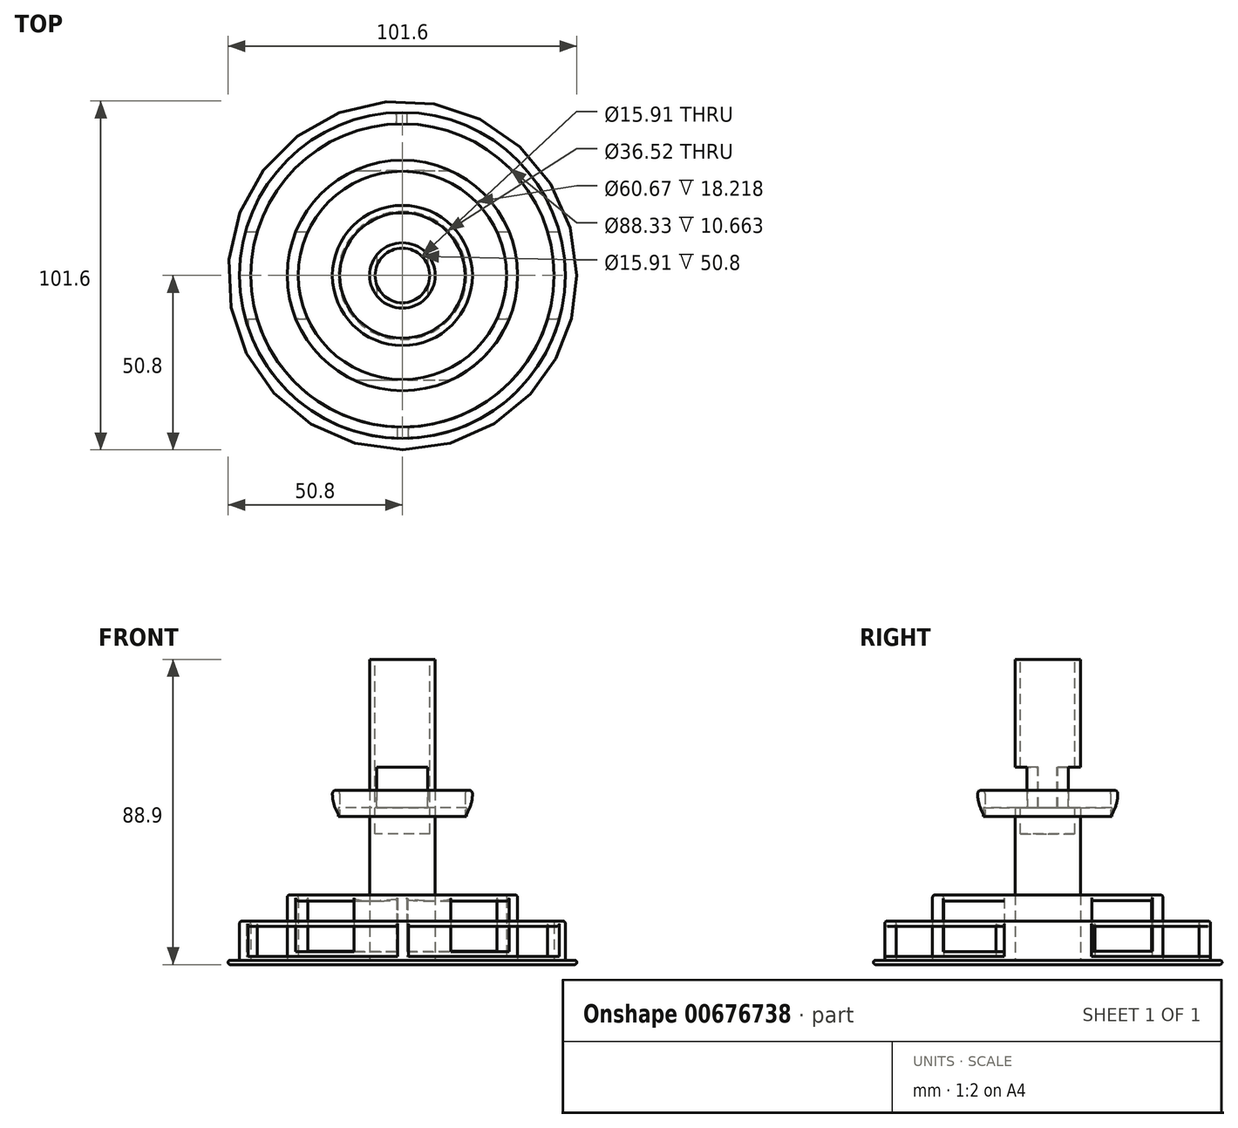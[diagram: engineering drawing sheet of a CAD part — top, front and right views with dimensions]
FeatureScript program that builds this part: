
annotation { "Feature Type Name" : "Feature", "Feature Type Description" : "" }
export const myFeature = defineFeature(function(context is Context, id is Id, definition is map)
    precondition{}
    {
        {
            var Q0;
            Q0=qCreatedBy(makeId("Top.planeOp"),FACE);
            var sketch = newSketch(context, id + "F0", { "sketchPlane" : qUnion([Q0])});
            skCircle(sketch, "E0", {"center": v(0, 0) * mm, "radius": 9.54 * mm});
            skSolve(sketch);
        }
        {
            var Q0;
            Q0 = qSketchRegion(id + "F0", true);
            extrude(context, id + "F1", {"entities" : qUnion([Q0]), "depth" : 88.9 * mm, "offsetDistance" : 25.4 * mm});
        }
        {
            var Q0;
            Q0=qCreatedBy(makeId("Top.planeOp"),FACE);
            var sketch = newSketch(context, id + "F2", { "sketchPlane" : qUnion([Q0])});
            skCircle(sketch, "E1", {"center": v(0, 0) * mm, "radius": 50.8 * mm});
            skSolve(sketch);
        }
        {
            var Q0;
            Q0 = qSketchRegion(id + "F2", true);
            extrude(context, id + "F3", {"entities" : qUnion([Q0]), "operationType" : NewBodyOperationType.ADD, "depth" : 1.27 * mm, "offsetDistance" : 25.4 * mm});
        }
        {
            var Q0;
            Q0=qCreatedBy(makeId("Top.planeOp"),FACE);
            var sketch = newSketch(context, id + "F4", { "sketchPlane" : qUnion([Q0])});
            skCircle(sketch, "E2", {"center": v(0, 0) * mm, "radius": 47.46 * mm});
            skCircle(sketch, "E3", {"center": v(0, 0) * mm, "radius": 44.16 * mm});
            skSolve(sketch);
        }
        {
            var Q0;
            Q0 = qSketchRegion(id + "F4", true);
            extrude(context, id + "F5", {"entities" : qUnion([Q0]), "operationType" : NewBodyOperationType.ADD, "depth" : 12.7 * mm, "offsetDistance" : 25.4 * mm});
        }
        {
            var Q0;
            Q0=qCreatedBy(makeId("Front.planeOp"),FACE);
            var sketch = newSketch(context, id + "F6", { "sketchPlane" : qUnion([Q0])});
            skLineSegment(sketch, "E4.bottom", {"start": v(-45.02, 11.17) * mm, "end": v(-1.38, 11.17) * mm});
            skLineSegment(sketch, "E4.top", {"start": v(-45.02, 2.4) * mm, "end": v(-1.38, 2.4) * mm});
            skLineSegment(sketch, "E4.left", {"start": v(-45.02, 11.17) * mm, "end": v(-45.02, 2.4) * mm});
            skLineSegment(sketch, "E4.right", {"start": v(-1.38, 11.17) * mm, "end": v(-1.38, 2.4) * mm});
            skLineSegment(sketch, "E5.bottom", {"start": v(1.72, 11.17) * mm, "end": v(46.37, 11.17) * mm});
            skLineSegment(sketch, "E5.top", {"start": v(1.72, 2.4) * mm, "end": v(46.37, 2.4) * mm});
            skLineSegment(sketch, "E5.left", {"start": v(1.72, 11.17) * mm, "end": v(1.72, 2.4) * mm});
            skLineSegment(sketch, "E5.right", {"start": v(46.37, 11.17) * mm, "end": v(46.37, 2.4) * mm});
            skSolve(sketch);
        }
        {
            var Q0;
            Q0 = qSketchRegion(id + "F6", true);
            extrude(context, id + "F7", {"entities" : qUnion([Q0]), "operationType" : NewBodyOperationType.REMOVE, "endBound" : BoundingType.THROUGH_ALL, "depth" : 25.4 * mm, "offsetDistance" : 25.4 * mm, "hasSecondDirection" : true, "secondDirectionOppositeDirection" : false, "secondDirectionDepth" : 12.7 * mm});
        }
        {
            var Q0;
            Q0=qCreatedBy(makeId("Front.planeOp"),FACE);
            var sketch = newSketch(context, id + "F8", { "sketchPlane" : qUnion([Q0])});
            skLineSegment(sketch, "E6.bottom", {"start": v(-45.43, 11.1) * mm, "end": v(-1.79, 11.1) * mm});
            skLineSegment(sketch, "E6.top", {"start": v(-45.43, 2.35) * mm, "end": v(-1.79, 2.35) * mm});
            skLineSegment(sketch, "E6.left", {"start": v(-45.43, 11.1) * mm, "end": v(-45.43, 2.35) * mm});
            skLineSegment(sketch, "E6.right", {"start": v(-1.79, 11.1) * mm, "end": v(-1.79, 2.35) * mm});
            skLineSegment(sketch, "E7.bottom", {"start": v(1.31, 11.1) * mm, "end": v(45.96, 11.1) * mm});
            skLineSegment(sketch, "E7.top", {"start": v(1.31, 2.35) * mm, "end": v(45.96, 2.35) * mm});
            skLineSegment(sketch, "E7.left", {"start": v(1.31, 11.1) * mm, "end": v(1.31, 2.35) * mm});
            skLineSegment(sketch, "E7.right", {"start": v(45.96, 11.1) * mm, "end": v(45.96, 2.35) * mm});
            skSolve(sketch);
        }
        {
            var Q0;
            Q0 = qSketchRegion(id + "F8", true);
            extrude(context, id + "F9", {"entities" : qUnion([Q0]), "operationType" : NewBodyOperationType.REMOVE, "endBound" : BoundingType.THROUGH_ALL, "oppositeDirection" : true, "depth" : 25.4 * mm, "offsetDistance" : 25.4 * mm, "hasSecondDirection" : true, "secondDirectionOppositeDirection" : true, "secondDirectionDepth" : 12.7 * mm});
        }
        {
            var Q0;
            Q0=qCreatedBy(makeId("Top.planeOp"),FACE);
            var sketch = newSketch(context, id + "F10", { "sketchPlane" : qUnion([Q0])});
            skCircle(sketch, "E8", {"center": v(0, 0) * mm, "radius": 33.57 * mm});
            skCircle(sketch, "E9", {"center": v(0, 0) * mm, "radius": 30.33 * mm});
            skSolve(sketch);
        }
        {
            var Q0;
            Q0 = qSketchRegion(id + "F10", true);
            extrude(context, id + "F11", {"entities" : qUnion([Q0]), "operationType" : NewBodyOperationType.ADD, "depth" : 20.32 * mm, "offsetDistance" : 25.4 * mm});
        }
        {
            var Q0;
            Q0=qCreatedBy(makeId("Front.planeOp"),FACE);
            var sketch = newSketch(context, id + "F12", { "sketchPlane" : qUnion([Q0])});
            skLineSegment(sketch, "E10.bottom", {"start": v(-31.36, 18.65) * mm, "end": v(-1.64, 18.65) * mm});
            skLineSegment(sketch, "E10.top", {"start": v(-31.36, 3.92) * mm, "end": v(-1.64, 3.92) * mm});
            skLineSegment(sketch, "E10.left", {"start": v(-31.36, 18.65) * mm, "end": v(-31.36, 3.92) * mm});
            skLineSegment(sketch, "E10.right", {"start": v(-1.64, 18.65) * mm, "end": v(-1.64, 3.92) * mm});
            skLineSegment(sketch, "E11.bottom", {"start": v(1.3, 18.62) * mm, "end": v(31.03, 18.62) * mm});
            skLineSegment(sketch, "E11.top", {"start": v(1.3, 3.89) * mm, "end": v(31.03, 3.89) * mm});
            skLineSegment(sketch, "E11.left", {"start": v(1.3, 18.62) * mm, "end": v(1.3, 3.89) * mm});
            skLineSegment(sketch, "E11.right", {"start": v(31.03, 18.62) * mm, "end": v(31.03, 3.89) * mm});
            skSolve(sketch);
        }
        {
            var Q0;
            Q0 = qSketchRegion(id + "F12", true);
            extrude(context, id + "F13", {"entities" : qUnion([Q0]), "operationType" : NewBodyOperationType.REMOVE, "oppositeDirection" : true, "depth" : 30.48 * mm, "offsetDistance" : 25.4 * mm, "hasSecondDirection" : true, "secondDirectionOppositeDirection" : true, "secondDirectionDepth" : 12.7 * mm});
        }
        {
            var Q0;
            Q0=qCreatedBy(makeId("Front.planeOp"),FACE);
            var sketch = newSketch(context, id + "F14", { "sketchPlane" : qUnion([Q0])});
            skLineSegment(sketch, "E12.bottom", {"start": v(-31.2, 18.52) * mm, "end": v(-1.47, 18.52) * mm});
            skLineSegment(sketch, "E12.top", {"start": v(-31.2, 3.8) * mm, "end": v(-1.47, 3.8) * mm});
            skLineSegment(sketch, "E12.left", {"start": v(-31.2, 18.52) * mm, "end": v(-31.2, 3.8) * mm});
            skLineSegment(sketch, "E12.right", {"start": v(-1.47, 18.52) * mm, "end": v(-1.47, 3.8) * mm});
            skLineSegment(sketch, "E13.bottom", {"start": v(1.47, 18.49) * mm, "end": v(31.2, 18.49) * mm});
            skLineSegment(sketch, "E13.top", {"start": v(1.47, 3.75) * mm, "end": v(31.2, 3.75) * mm});
            skLineSegment(sketch, "E13.left", {"start": v(1.47, 18.49) * mm, "end": v(1.47, 3.75) * mm});
            skLineSegment(sketch, "E13.right", {"start": v(31.2, 18.49) * mm, "end": v(31.2, 3.75) * mm});
            skSolve(sketch);
        }
        {
            var Q0;
            Q0 = qSketchRegion(id + "F14", true);
            extrude(context, id + "F15", {"entities" : qUnion([Q0]), "operationType" : NewBodyOperationType.REMOVE, "depth" : 30.48 * mm, "offsetDistance" : 25.4 * mm, "hasSecondDirection" : true, "secondDirectionOppositeDirection" : false, "secondDirectionDepth" : 12.7 * mm});
        }
        {
            var Q0;
            Q0=qCreatedBy(makeId("Front.planeOp"),FACE);
            var sketch = newSketch(context, id + "F16", { "sketchPlane" : qUnion([Q0])});
            skLineSegment(sketch, "E14.bottom", {"start": v(-7.47, 57.44) * mm, "end": v(7.4, 57.44) * mm});
            skLineSegment(sketch, "E14.top", {"start": v(-7.47, 45.71) * mm, "end": v(7.4, 45.71) * mm});
            skLineSegment(sketch, "E14.left", {"start": v(-7.47, 57.44) * mm, "end": v(-7.47, 45.71) * mm});
            skLineSegment(sketch, "E14.right", {"start": v(7.4, 57.44) * mm, "end": v(7.4, 45.71) * mm});
            skSolve(sketch);
        }
        {
            var Q0;
            Q0 = qSketchRegion(id + "F16", true);
            extrude(context, id + "F17", {"entities" : qUnion([Q0]), "operationType" : NewBodyOperationType.REMOVE, "oppositeDirection" : true, "depth" : 25.4 * mm, "offsetDistance" : 25.4 * mm});
        }
        {
            var Q0;
            Q0 = qSketchRegion(id + "F16", true);
            extrude(context, id + "F18", {"entities" : qUnion([Q0]), "operationType" : NewBodyOperationType.REMOVE, "depth" : 25.4 * mm, "offsetDistance" : 25.4 * mm});
        }
        {
            var Q0;
            Q0=qCreatedBy(makeId("Top.planeOp"),FACE);
            var sketch = newSketch(context, id + "F19", { "sketchPlane" : qUnion([Q0])});
            skCircle(sketch, "E15", {"center": v(0, 0) * mm, "radius": 20.4 * mm});
            skCircle(sketch, "E16", {"center": v(0, 0) * mm, "radius": 18.26 * mm});
            skSolve(sketch);
        }
        {
            var Q0;
            Q0 = qSketchRegion(id + "F19", true);
            extrude(context, id + "F20", {"entities" : qUnion([Q0]), "depth" : 50.8 * mm, "offsetDistance" : 25.4 * mm, "hasSecondDirection" : true, "secondDirectionOppositeDirection" : false, "secondDirectionDepth" : 43.18 * mm});
        }
        {
            var Q0;
            Q0=qCreatedBy(makeId("Top.planeOp"),FACE);
            var sketch = newSketch(context, id + "F21", { "sketchPlane" : qUnion([Q0])});
            skCircle(sketch, "E17", {"center": v(0, 0) * mm, "radius": 18.7 * mm});
            skSolve(sketch);
        }
        {
            var Q0;
            Q0 = qSketchRegion(id + "F21", true);
            extrude(context, id + "F22", {"entities" : qUnion([Q0]), "depth" : 45.72 * mm, "offsetDistance" : 25.4 * mm, "hasSecondDirection" : true, "secondDirectionOppositeDirection" : false, "secondDirectionDepth" : 43.18 * mm});
        }
        {
            var Q0;
            Q0=makeQuery(id+"F1.opExtrude","CAP_FACE",FACE,{"disambiguationData":[OSD([sQuery(id+"F0.wireOp",EDGE,"E0")])],"isStart":false});
            var sketch = newSketch(context, id + "F23", { "sketchPlane" : qUnion([Q0])});
            skCircle(sketch, "E18", {"center": v(0, 0) * mm, "radius": 7.96 * mm});
            skSolve(sketch);
        }
        {
            var Q0;
            Q0 = qSketchRegion(id + "F23", true);
            extrude(context, id + "F24", {"entities" : qUnion([Q0]), "operationType" : NewBodyOperationType.REMOVE, "oppositeDirection" : true, "depth" : 50.8 * mm, "offsetDistance" : 25.4 * mm});
        }
        {
            var Q0;
            Q0=makeQuery(id+"F20.opExtrude","CAP_EDGE",EDGE,{"disambiguationData":[OSD([sQuery(id+"F19.wireOp",EDGE,"E15")])],"isStart":false});
            var Q1;
            Q1=makeQuery(id+"F20.opExtrude","CAP_EDGE",EDGE,{"disambiguationData":[OSD([sQuery(id+"F19.wireOp",EDGE,"E16")])],"isStart":false});
            fillet(context, id + "F25", {"entities" : qUnion([Q0, Q1]), "radius" : 1.07 * mm, "tangentPropagation" : true, "allowEdgeOverflow" : false});
        }
        {
            var Q0;
            Q0=makeQuery(id+"F11.opExtrude","CAP_EDGE",EDGE,{"disambiguationData":[OSD([sQuery(id+"F10.wireOp",EDGE,"E8")])],"isStart":false});
            var Q1;
            Q1=makeQuery(id+"F11.opExtrude","CAP_EDGE",EDGE,{"disambiguationData":[OSD([sQuery(id+"F10.wireOp",EDGE,"E9")])],"isStart":false});
            var Q2;
            Q2=makeQuery(id+"F15.boolean.opBoolean","INTERSECT",EDGE,{"derivedFrom":[makeQuery(id+"F11.opExtrude","SWEPT_FACE",FACE,{"disambiguationData":[OSD([sQuery(id+"F10.wireOp",EDGE,"E9")])]}),makeQuery(id+"F15.opExtrude","SWEPT_FACE",FACE,{"disambiguationData":[OSD([sQuery(id+"F14.wireOp",EDGE,"E12.bottom")])]})]});
            var Q3;
            Q3=makeQuery(id+"F15.boolean.opBoolean","INTERSECT",EDGE,{"derivedFrom":[makeQuery(id+"F11.opExtrude","SWEPT_FACE",FACE,{"disambiguationData":[OSD([sQuery(id+"F10.wireOp",EDGE,"E8")])]}),makeQuery(id+"F15.opExtrude","SWEPT_FACE",FACE,{"disambiguationData":[OSD([sQuery(id+"F14.wireOp",EDGE,"E12.bottom")])]})]});
            var Q4;
            Q4=makeQuery(id+"F13.boolean.opBoolean","INTERSECT",EDGE,{"derivedFrom":[makeQuery(id+"F11.opExtrude","SWEPT_FACE",FACE,{"disambiguationData":[OSD([sQuery(id+"F10.wireOp",EDGE,"E9")])]}),makeQuery(id+"F13.opExtrude","SWEPT_FACE",FACE,{"disambiguationData":[OSD([sQuery(id+"F12.wireOp",EDGE,"E10.bottom")])]})]});
            var Q5;
            Q5=makeQuery(id+"F13.boolean.opBoolean","INTERSECT",EDGE,{"derivedFrom":[makeQuery(id+"F11.opExtrude","SWEPT_FACE",FACE,{"disambiguationData":[OSD([sQuery(id+"F10.wireOp",EDGE,"E8")])]}),makeQuery(id+"F13.opExtrude","SWEPT_FACE",FACE,{"disambiguationData":[OSD([sQuery(id+"F12.wireOp",EDGE,"E10.bottom")])]})]});
            var Q6;
            Q6=makeQuery(id+"F13.boolean.opBoolean","INTERSECT",EDGE,{"derivedFrom":[makeQuery(id+"F11.opExtrude","SWEPT_FACE",FACE,{"disambiguationData":[OSD([sQuery(id+"F10.wireOp",EDGE,"E9")])]}),makeQuery(id+"F13.opExtrude","SWEPT_FACE",FACE,{"disambiguationData":[OSD([sQuery(id+"F12.wireOp",EDGE,"E11.bottom")])]})]});
            var Q7;
            Q7=makeQuery(id+"F13.boolean.opBoolean","INTERSECT",EDGE,{"derivedFrom":[makeQuery(id+"F11.opExtrude","SWEPT_FACE",FACE,{"disambiguationData":[OSD([sQuery(id+"F10.wireOp",EDGE,"E8")])]}),makeQuery(id+"F13.opExtrude","SWEPT_FACE",FACE,{"disambiguationData":[OSD([sQuery(id+"F12.wireOp",EDGE,"E11.bottom")])]})]});
            var Q8;
            Q8=makeQuery(id+"F15.boolean.opBoolean","INTERSECT",EDGE,{"derivedFrom":[makeQuery(id+"F11.opExtrude","SWEPT_FACE",FACE,{"disambiguationData":[OSD([sQuery(id+"F10.wireOp",EDGE,"E8")])]}),makeQuery(id+"F15.opExtrude","SWEPT_FACE",FACE,{"disambiguationData":[OSD([sQuery(id+"F14.wireOp",EDGE,"E13.bottom")])]})]});
            var Q9;
            Q9=makeQuery(id+"F15.boolean.opBoolean","INTERSECT",EDGE,{"derivedFrom":[makeQuery(id+"F11.opExtrude","SWEPT_FACE",FACE,{"disambiguationData":[OSD([sQuery(id+"F10.wireOp",EDGE,"E9")])]}),makeQuery(id+"F15.opExtrude","SWEPT_FACE",FACE,{"disambiguationData":[OSD([sQuery(id+"F14.wireOp",EDGE,"E13.bottom")])]})]});
            fillet(context, id + "F26", {"entities" : qUnion([Q0, Q1, Q2, Q3, Q4, Q5, Q6, Q7, Q8, Q9]), "radius" : 0.83 * mm, "tangentPropagation" : true, "allowEdgeOverflow" : false});
        }
        {
            var Q0;
            Q0=makeQuery(id+"F5.opExtrude","CAP_EDGE",EDGE,{"disambiguationData":[OSD([sQuery(id+"F4.wireOp",EDGE,"E3")])],"isStart":false});
            var Q1;
            Q1=makeQuery(id+"F5.opExtrude","CAP_EDGE",EDGE,{"disambiguationData":[OSD([sQuery(id+"F4.wireOp",EDGE,"E2")])],"isStart":false});
            var Q2;
            Q2=makeQuery(id+"F7.boolean.opBoolean","INTERSECT",EDGE,{"derivedFrom":[makeQuery(id+"F5.opExtrude","SWEPT_FACE",FACE,{"disambiguationData":[OSD([sQuery(id+"F4.wireOp",EDGE,"E2")])]}),makeQuery(id+"F7.opExtrude","SWEPT_FACE",FACE,{"disambiguationData":[OSD([sQuery(id+"F6.wireOp",EDGE,"E5.bottom")])]})]});
            var Q3;
            Q3=makeQuery(id+"F7.boolean.opBoolean","INTERSECT",EDGE,{"derivedFrom":[makeQuery(id+"F5.opExtrude","SWEPT_FACE",FACE,{"disambiguationData":[OSD([sQuery(id+"F4.wireOp",EDGE,"E3")])]}),makeQuery(id+"F7.opExtrude","SWEPT_FACE",FACE,{"disambiguationData":[OSD([sQuery(id+"F6.wireOp",EDGE,"E5.bottom")])]})]});
            var Q4;
            Q4=makeQuery(id+"F7.boolean.opBoolean","INTERSECT",EDGE,{"derivedFrom":[makeQuery(id+"F5.opExtrude","SWEPT_FACE",FACE,{"disambiguationData":[OSD([sQuery(id+"F4.wireOp",EDGE,"E3")])]}),makeQuery(id+"F7.opExtrude","SWEPT_FACE",FACE,{"disambiguationData":[OSD([sQuery(id+"F6.wireOp",EDGE,"E4.bottom")])]})]});
            var Q5;
            Q5=makeQuery(id+"F7.boolean.opBoolean","INTERSECT",EDGE,{"derivedFrom":[makeQuery(id+"F5.opExtrude","SWEPT_FACE",FACE,{"disambiguationData":[OSD([sQuery(id+"F4.wireOp",EDGE,"E2")])]}),makeQuery(id+"F7.opExtrude","SWEPT_FACE",FACE,{"disambiguationData":[OSD([sQuery(id+"F6.wireOp",EDGE,"E4.bottom")])]})]});
            var Q6;
            Q6=makeQuery(id+"F9.boolean.opBoolean","INTERSECT",EDGE,{"derivedFrom":[makeQuery(id+"F5.opExtrude","SWEPT_FACE",FACE,{"disambiguationData":[OSD([sQuery(id+"F4.wireOp",EDGE,"E3")])]}),makeQuery(id+"F9.opExtrude","SWEPT_FACE",FACE,{"disambiguationData":[OSD([sQuery(id+"F8.wireOp",EDGE,"E6.bottom")])]})]});
            var Q7;
            Q7=makeQuery(id+"F9.boolean.opBoolean","INTERSECT",EDGE,{"derivedFrom":[makeQuery(id+"F5.opExtrude","SWEPT_FACE",FACE,{"disambiguationData":[OSD([sQuery(id+"F4.wireOp",EDGE,"E2")])]}),makeQuery(id+"F9.opExtrude","SWEPT_FACE",FACE,{"disambiguationData":[OSD([sQuery(id+"F8.wireOp",EDGE,"E6.bottom")])]})]});
            var Q8;
            Q8=makeQuery(id+"F9.boolean.opBoolean","INTERSECT",EDGE,{"derivedFrom":[makeQuery(id+"F5.opExtrude","SWEPT_FACE",FACE,{"disambiguationData":[OSD([sQuery(id+"F4.wireOp",EDGE,"E3")])]}),makeQuery(id+"F9.opExtrude","SWEPT_FACE",FACE,{"disambiguationData":[OSD([sQuery(id+"F8.wireOp",EDGE,"E7.bottom")])]})]});
            var Q9;
            Q9=makeQuery(id+"F9.boolean.opBoolean","INTERSECT",EDGE,{"derivedFrom":[makeQuery(id+"F5.opExtrude","SWEPT_FACE",FACE,{"disambiguationData":[OSD([sQuery(id+"F4.wireOp",EDGE,"E2")])]}),makeQuery(id+"F9.opExtrude","SWEPT_FACE",FACE,{"disambiguationData":[OSD([sQuery(id+"F8.wireOp",EDGE,"E7.bottom")])]})]});
            fillet(context, id + "F27", {"entities" : qUnion([Q0, Q1, Q2, Q3, Q4, Q5, Q6, Q7, Q8, Q9]), "radius" : 0.77 * mm, "tangentPropagation" : true, "allowEdgeOverflow" : false});
        }
        {
            var Q0;
            Q0=makeQuery(id+"F20.opExtrude","CAP_EDGE",EDGE,{"disambiguationData":[OSD([sQuery(id+"F19.wireOp",EDGE,"E15")])],"isStart":true});
            fillet(context, id + "F28", {"entities" : qUnion([Q0]), "radius" : 11.07 * mm, "tangentPropagation" : true, "allowEdgeOverflow" : false});
        }
        {
            var Q0;
            Q0=makeQuery(id+"F3.opExtrude","CAP_EDGE",EDGE,{"disambiguationData":[OSD([sQuery(id+"F2.wireOp",EDGE,"E1")])],"isStart":false});
            var Q1;
            Q1=makeQuery(id+"F3.opExtrude","CAP_EDGE",EDGE,{"disambiguationData":[OSD([sQuery(id+"F2.wireOp",EDGE,"E1")])],"isStart":true});
            fillet(context, id + "F29", {"entities" : qUnion([Q0, Q1]), "radius" : 0.64 * mm, "tangentPropagation" : true, "allowEdgeOverflow" : false});
        }
    });
